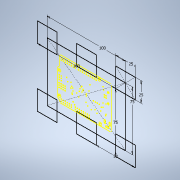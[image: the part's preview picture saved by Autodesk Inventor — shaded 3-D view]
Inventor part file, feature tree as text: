
AUTODESK INVENTOR PART (.ipt)
format: ipt  version: 2021 (Build 250183000, 183)  size: 372,224 bytes
history: native  units: mm
features: reference x4, other x3, extrude x1, sketch x1
ambient origin geometry x8: Origin, YZ Plane, XZ Plane, XY Plane, X Axis, Y Axis, Z Axis, Center Point
bodies: Solid1 (feature_tree)
feature tree (9):
  extrude  "Extrusion1"  Depth=90.0mm
  sketch  "Sketch1"  dims[d0=100.0mm d1=90.0mm d2=25.0mm d3=25.0mm d4=20.0mm d6=90.0mm d7=20.0mm d9=100.0mm d12=20.0mm d14=50.0mm d15=10.0mm d17=10.0mm d19=40.0mm d20=40.0mm d21=0.308648mm d22=10.0mm d23=0.0mm]
  reference  "Reference1"
  reference  "Reference2"
  reference  "Reference3"
  reference  "Reference4"
  other  "Ensamble_del_hexapod_V1.iam"
  other  "Arduino UNO Rev.3 (CH340)-CAWEB.ORG:1"
  other  "PCB:1"
